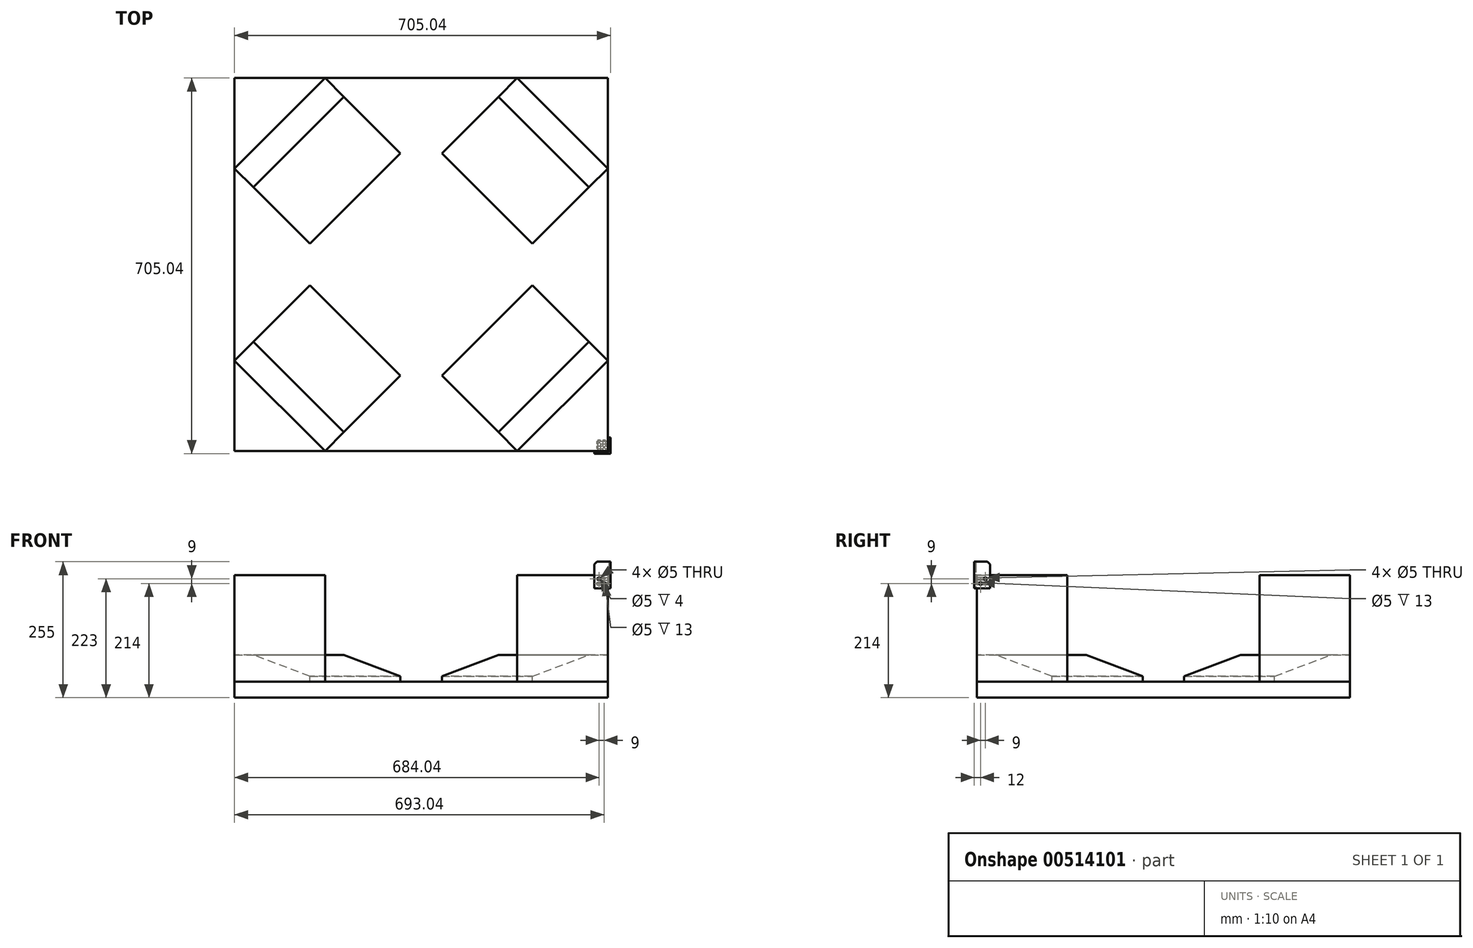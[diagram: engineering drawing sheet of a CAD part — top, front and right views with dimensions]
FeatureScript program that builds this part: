
annotation { "Feature Type Name" : "Feature", "Feature Type Description" : "" }
export const myFeature = defineFeature(function(context is Context, id is Id, definition is map)
    precondition{}
    {
        {
            var Q0;
            Q0=qCreatedBy(makeId("Top.planeOp"),FACE);
            var sketch = newSketch(context, id + "F0", { "sketchPlane" : qUnion([Q0])});
            skLineSegment(sketch, "E0.bottom", {"start": v(-350, 350) * mm, "end": v(350, 350) * mm});
            skLineSegment(sketch, "E0.top", {"start": v(-350, -350) * mm, "end": v(350, -350) * mm});
            skLineSegment(sketch, "E0.left", {"start": v(-350, 350) * mm, "end": v(-350, -350) * mm});
            skLineSegment(sketch, "E0.right", {"start": v(350, 350) * mm, "end": v(350, -350) * mm});
            skLineSegment(sketch, "E1", {"start": v(0, 350) * mm, "end": v(0, -350) * mm, "construction": true});
            skLineSegment(sketch, "E2", {"start": v(-350, 0) * mm, "end": v(350, 0) * mm, "construction": true});
            skSolve(sketch);
        }
        {
            var Q0;
            Q0=makeQuery(id+"F0.imprint","IMPRINT",FACE,{"disambiguationData":[TD([[makeQuery(id+"F0.imprint","IMPRINT",EDGE,{"derivedFrom":sQuery(id+"F0.wireOp",EDGE,"E0.bottom")}),-1.0]])]});
            extrude(context, id + "F1", {"entities" : qUnion([Q0]), "oppositeDirection" : true, "depth" : 30 * mm});
        }
        {
            var Q0;
            Q0=makeQuery(id+"F1.opExtrude","CAP_FACE",FACE,{"disambiguationData":[OSD([sQuery(id+"F0.wireOp",EDGE,"E0.bottom"),sQuery(id+"F0.wireOp",EDGE,"E0.top"),sQuery(id+"F0.wireOp",EDGE,"E0.left"),sQuery(id+"F0.wireOp",EDGE,"E0.right")])],"isStart":true});
            var sketch = newSketch(context, id + "F2", { "sketchPlane" : qUnion([Q0])});
            skLineSegment(sketch, "E3", {"start": v(-350, -180.33) * mm, "end": v(-180.33, -350) * mm});
            skLineSegment(sketch, "E4", {"start": v(-350, -350) * mm, "end": v(0, 0) * mm, "construction": true});
            skLineSegment(sketch, "E5", {"start": v(0, 0) * mm, "end": v(350, -350) * mm, "construction": true});
            skLineSegment(sketch, "E6", {"start": v(180.33, 350) * mm, "end": v(350, 180.33) * mm, "construction": true});
            skSolve(sketch);
        }
        {
            var Q0;
            {var subQ0=sQuery(id+"F2.wireOp",EDGE,"E3");Q0=makeQuery(id+"F2.imprint","IMPRINT",FACE,{"disambiguationData":[TD([[makeQuery(id+"F2.imprint","IMPRINT",EDGE,{"derivedFrom":subQ0}),-1.0]])]});}
            extrude(context, id + "F3", {"entities" : qUnion([Q0]), "depth" : 200 * mm});
        }
        {
            var Q0;
            Q0=makeQuery(id+"F3.opExtrude","SWEPT_EDGE",EDGE,{"disambiguationData":[OSD([sQuery(id+"F0.wireOp",EDGE,"E0.top"),sQuery(id+"F2.wireOp",EDGE,"E3")])]});
            cPlane(context, id + "F4", {"entities" : qUnion([Q0]), "cplaneType" : CPlaneType.LINE_ANGLE, "offset" : 25 * mm, "angle" : 45 * degree, "width" : 150 * mm, "height" : 150 * mm});
        }
        {
            var Q0;
            Q0=qCreatedBy(id+"F4.planeOp",FACE);
            var sketch = newSketch(context, id + "F5", { "sketchPlane" : qUnion([Q0])});
            skLineSegment(sketch, "E7.0", {"start": v(375, 200) * mm, "end": v(375, 0) * mm});
            skLineSegment(sketch, "E8.0", {"start": v(494.97, 0) * mm, "end": v(0, 0) * mm});
            skLineSegment(sketch, "E9", {"start": v(375, 50) * mm, "end": v(325, 50) * mm});
            skLineSegment(sketch, "E10", {"start": v(175, 0) * mm, "end": v(175, 10) * mm});
            skLineSegment(sketch, "E11", {"start": v(175, 10) * mm, "end": v(325, 50) * mm});
            skSolve(sketch);
        }
        {
            var Q0;
            {var subQ1=sQuery(id+"F5.wireOp",EDGE,"E9");Q0=makeQuery(id+"F5.imprint","IMPRINT",FACE,{"disambiguationData":[TD([[makeQuery(id+"F5.imprint","IMPRINT",EDGE,{"derivedFrom":subQ1}),1.0]])]});}
            extrude(context, id + "F6", {"entities" : qUnion([Q0]), "depth" : 240 * mm});
        }
        {
            var Q0;
            Q0=qCreatedBy(makeId("Right.planeOp"),FACE);
            var sketch = newSketch(context, id + "F7", { "sketchPlane" : qUnion([Q0])});
            skLineSegment(sketch, "E12", {"start": v(0, 0) * mm, "end": v(0, 300) * mm, "construction": true});
            skSolve(sketch);
        }
        {
            var Q0;
            Q0=makeQuery(id+"F3.opExtrude","SWEPT_BODY",BODY,{"disambiguationData":[OSD([sQuery(id+"F0.wireOp",EDGE,"E0.top"),sQuery(id+"F0.wireOp",EDGE,"E0.left"),sQuery(id+"F2.wireOp",EDGE,"E3")])]});
            var Q1;
            Q1=sQuery(id+"F7.wireOp",EDGE,"E12");
            transform(context, id + "F8", {"entities" : qUnion([Q0]), "transformType" : TransformType.ROTATION, "transformAxis" : qUnion([Q1]), "angle" : 90 * degree, "makeCopy" : true});
        }
        {
            var Q0;
            Q0=makeQuery(id+"F3.opExtrude","SWEPT_BODY",BODY,{"disambiguationData":[OSD([sQuery(id+"F0.wireOp",EDGE,"E0.top"),sQuery(id+"F0.wireOp",EDGE,"E0.left"),sQuery(id+"F2.wireOp",EDGE,"E3")])]});
            var Q1;
            Q1=sQuery(id+"F7.wireOp",EDGE,"E12");
            transform(context, id + "F9", {"entities" : qUnion([Q0]), "transformType" : TransformType.ROTATION, "transformAxis" : qUnion([Q1]), "angle" : 180 * degree, "makeCopy" : true});
        }
        {
            var Q0;
            Q0=makeQuery(id+"F3.opExtrude","SWEPT_BODY",BODY,{"disambiguationData":[OSD([sQuery(id+"F0.wireOp",EDGE,"E0.top"),sQuery(id+"F0.wireOp",EDGE,"E0.left"),sQuery(id+"F2.wireOp",EDGE,"E3")])]});
            var Q1;
            Q1=sQuery(id+"F7.wireOp",EDGE,"E12");
            transform(context, id + "F10", {"entities" : qUnion([Q0]), "transformType" : TransformType.ROTATION, "transformAxis" : qUnion([Q1]), "angle" : 270 * degree, "makeCopy" : true});
        }
        {
            var Q0;
            Q0=makeQuery(id+"F6.opExtrude","SWEPT_BODY",BODY,{"disambiguationData":[OSD([sQuery(id+"F5.wireOp",EDGE,"E7.0"),sQuery(id+"F5.wireOp",EDGE,"E8.0"),sQuery(id+"F5.wireOp",EDGE,"QHIc2Bnu-9Cy2-sG9u-M0cL-EqV01xjCvLUi")])]});
            var Q1;
            Q1=sQuery(id+"F7.wireOp",EDGE,"E12");
            transform(context, id + "F11", {"entities" : qUnion([Q0]), "transformType" : TransformType.ROTATION, "transformAxis" : qUnion([Q1]), "angle" : 90 * degree, "makeCopy" : true});
        }
        {
            var Q0;
            Q0=makeQuery(id+"F6.opExtrude","SWEPT_BODY",BODY,{"disambiguationData":[OSD([sQuery(id+"F5.wireOp",EDGE,"E7.0"),sQuery(id+"F5.wireOp",EDGE,"E8.0"),sQuery(id+"F5.wireOp",EDGE,"QHIc2Bnu-9Cy2-sG9u-M0cL-EqV01xjCvLUi")])]});
            var Q1;
            Q1=sQuery(id+"F7.wireOp",EDGE,"E12");
            transform(context, id + "F12", {"entities" : qUnion([Q0]), "transformType" : TransformType.ROTATION, "transformAxis" : qUnion([Q1]), "angle" : 180 * degree, "makeCopy" : true});
        }
        {
            var Q0;
            Q0=makeQuery(id+"F6.opExtrude","SWEPT_BODY",BODY,{"disambiguationData":[OSD([sQuery(id+"F5.wireOp",EDGE,"E7.0"),sQuery(id+"F5.wireOp",EDGE,"E8.0"),sQuery(id+"F5.wireOp",EDGE,"QHIc2Bnu-9Cy2-sG9u-M0cL-EqV01xjCvLUi")])]});
            var Q1;
            Q1=sQuery(id+"F7.wireOp",EDGE,"E12");
            transform(context, id + "F13", {"entities" : qUnion([Q0]), "transformType" : TransformType.ROTATION, "transformAxis" : qUnion([Q1]), "angle" : 270 * degree, "makeCopy" : true});
        }
        {
            var Q0;
            Q0=makeQuery(id+"F8.opPattern","COPY",FACE,{"derivedFrom":makeQuery(id+"F3.opExtrude","CAP_FACE",FACE,{"disambiguationData":[OSD([sQuery(id+"F0.wireOp",EDGE,"E0.top"),sQuery(id+"F0.wireOp",EDGE,"E0.left"),sQuery(id+"F2.wireOp",EDGE,"E3")])],"isStart":false}),"instanceName":"1"});
            var sketch = newSketch(context, id + "F14", { "sketchPlane" : qUnion([Q0])});
            skLineSegment(sketch, "E13", {"start": v(352, -325) * mm, "end": v(352, -352) * mm});
            skLineSegment(sketch, "E14", {"start": v(352, -352) * mm, "end": v(325, -352) * mm});
            skLineSegment(sketch, "E15", {"start": v(325, -352) * mm, "end": v(325, -355) * mm});
            skLineSegment(sketch, "E16", {"start": v(325, -355) * mm, "end": v(355, -355) * mm});
            skLineSegment(sketch, "E17", {"start": v(355, -355) * mm, "end": v(355, -325) * mm});
            skLineSegment(sketch, "E18", {"start": v(355, -325) * mm, "end": v(352, -325) * mm});
            skSolve(sketch);
        }
        {
            var Q0;
            Q0=makeQuery(id+"F14.imprint","IMPRINT",FACE,{"disambiguationData":[TD([[makeQuery(id+"F14.imprint","IMPRINT",EDGE,{"derivedFrom":sQuery(id+"F14.wireOp",EDGE,"E13")}),1.0]])]});
            extrude(context, id + "F15", {"entities" : qUnion([Q0]), "depth" : 25 * mm, "offsetDistance" : 25 * mm, "hasSecondDirection" : true, "secondDirectionOppositeDirection" : true, "secondDirectionDepth" : 25 * mm});
        }
        {
            var Q0;
            Q0=makeQuery(id+"F15.opExtrude","SWEPT_FACE",FACE,{"disambiguationData":[OSD([sQuery(id+"F14.wireOp",EDGE,"E16")])]});
            var sketch = newSketch(context, id + "F16", { "sketchPlane" : qUnion([Q0])});
            skCircle(sketch, "E19", {"center": v(343, 184) * mm, "radius": 2.5 * mm});
            skCircle(sketch, "E20", {"center": v(334, 193) * mm, "radius": 2.5 * mm});
            skSolve(sketch);
        }
        {
            var Q0;
            Q0=makeQuery(id+"F15.opExtrude","SWEPT_FACE",FACE,{"disambiguationData":[OSD([sQuery(id+"F14.wireOp",EDGE,"E17")])]});
            var sketch = newSketch(context, id + "F17", { "sketchPlane" : qUnion([Q0])});
            skCircle(sketch, "E21", {"center": v(-343, 184) * mm, "radius": 2.5 * mm});
            skCircle(sketch, "E22", {"center": v(-334, 193) * mm, "radius": 2.5 * mm});
            skSolve(sketch);
        }
        {
            var Q0;
            Q0=makeQuery(id+"F17.imprint","IMPRINT",FACE,{"disambiguationData":[TD([[makeQuery(id+"F17.imprint","IMPRINT",EDGE,{"derivedFrom":sQuery(id+"F17.wireOp",EDGE,"E22")}),1.0]])]});
            var Q1;
            Q1=makeQuery(id+"F17.imprint","IMPRINT",FACE,{"disambiguationData":[TD([[makeQuery(id+"F17.imprint","IMPRINT",EDGE,{"derivedFrom":sQuery(id+"F17.wireOp",EDGE,"E21")}),1.0]])]});
            extrude(context, id + "F18", {"entities" : qUnion([Q0, Q1]), "operationType" : NewBodyOperationType.REMOVE, "oppositeDirection" : true, "depth" : 25 * mm, "offsetDistance" : 25 * mm});
        }
        {
            var Q0;
            Q0=makeQuery(id+"F16.imprint","IMPRINT",FACE,{"disambiguationData":[TD([[makeQuery(id+"F16.imprint","IMPRINT",EDGE,{"derivedFrom":sQuery(id+"F16.wireOp",EDGE,"E20")}),1.0]])]});
            var Q1;
            Q1=makeQuery(id+"F16.imprint","IMPRINT",FACE,{"disambiguationData":[TD([[makeQuery(id+"F16.imprint","IMPRINT",EDGE,{"derivedFrom":sQuery(id+"F16.wireOp",EDGE,"E19")}),1.0]])]});
            extrude(context, id + "F19", {"entities" : qUnion([Q0, Q1]), "operationType" : NewBodyOperationType.REMOVE, "oppositeDirection" : true, "depth" : 25 * mm, "offsetDistance" : 25 * mm});
        }
        {
            var Q0;
            Q0=makeQuery(id+"F15.opExtrude","CAP_EDGE",EDGE,{"disambiguationData":[OSD([sQuery(id+"F14.wireOp",EDGE,"E15")])],"isStart":false});
            var Q1;
            Q1=makeQuery(id+"F15.opExtrude","CAP_EDGE",EDGE,{"disambiguationData":[OSD([sQuery(id+"F14.wireOp",EDGE,"E18")])],"isStart":false});
            chamfer(context, id + "F20", {"entities" : qUnion([Q0, Q1]), "width" : 5 * mm, "tangentPropagation" : true});
        }
    });
